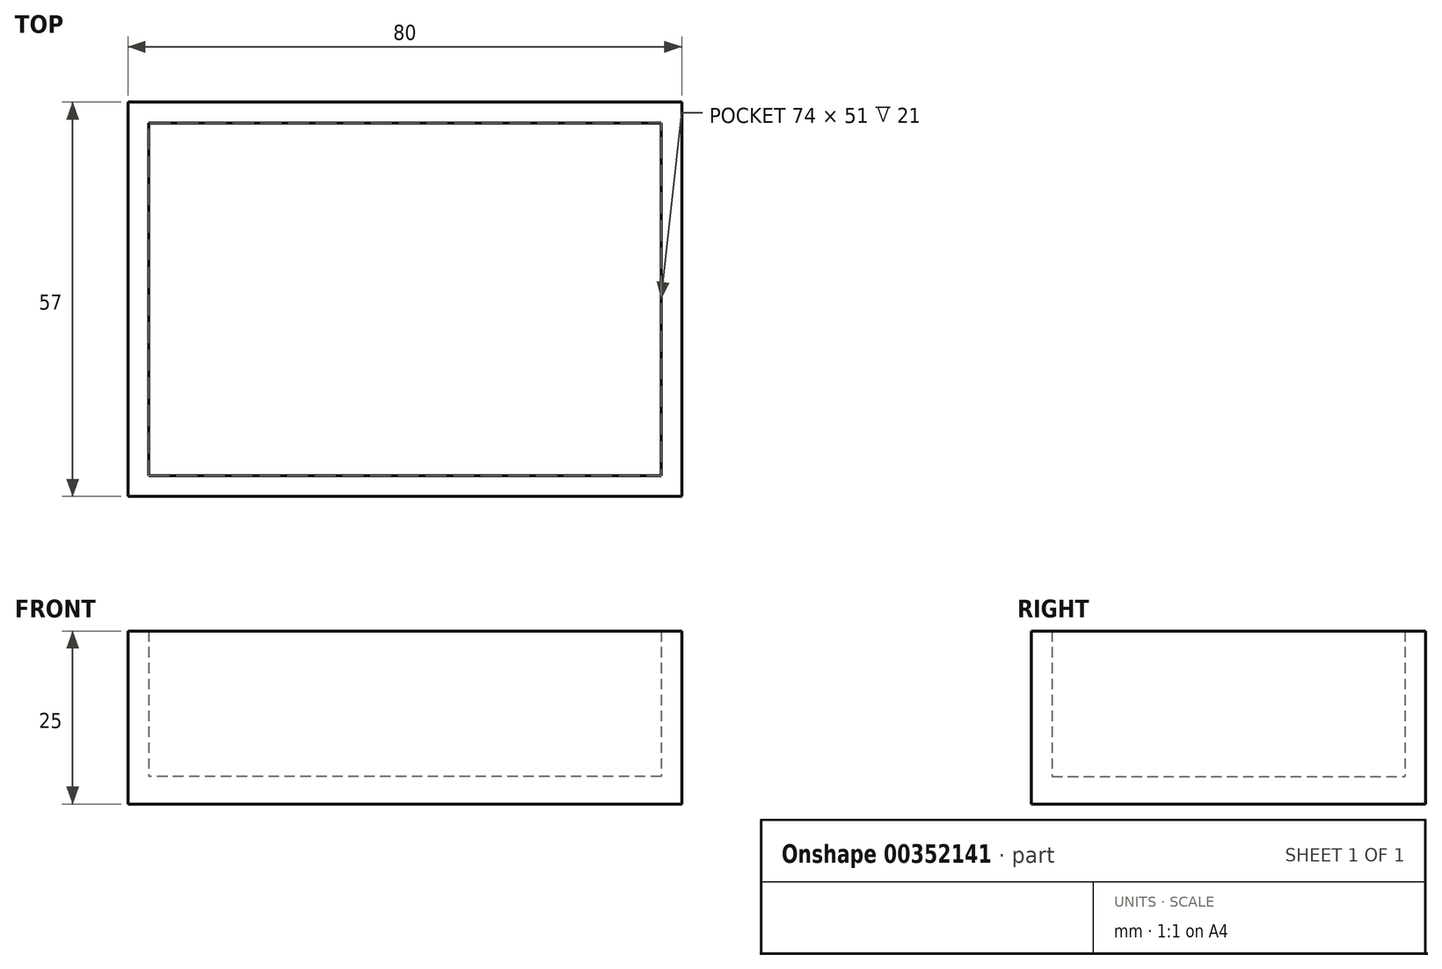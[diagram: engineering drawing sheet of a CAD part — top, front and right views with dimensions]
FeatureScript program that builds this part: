
annotation { "Feature Type Name" : "Feature", "Feature Type Description" : "" }
export const myFeature = defineFeature(function(context is Context, id is Id, definition is map)
    precondition{}
    {
        {
            var Q0;
            Q0=qCreatedBy(makeId("Top.planeOp"),FACE);
            var sketch = newSketch(context, id + "F0", { "sketchPlane" : qUnion([Q0])});
            skLineSegment(sketch, "E0.bottom", {"start": v(0, 0) * mm, "end": v(-80, 0) * mm});
            skLineSegment(sketch, "E0.left", {"start": v(0, 0) * mm, "end": v(0, 57) * mm});
            skPoint(sketch, "E1", {"position": v(-40, 28.5) * mm});
            skLineSegment(sketch, "E2.bottom", {"start": v(-77, 54) * mm, "end": v(-3, 54) * mm});
            skLineSegment(sketch, "E2.top", {"start": v(-77, 3) * mm, "end": v(-3, 3) * mm});
            skLineSegment(sketch, "E2.left", {"start": v(-77, 54) * mm, "end": v(-77, 3) * mm});
            skLineSegment(sketch, "E2.right", {"start": v(-3, 54) * mm, "end": v(-3, 3) * mm});
            skLineSegment(sketch, "E3.top", {"start": v(-80, 0) * mm, "end": v(0, 0) * mm});
            skLineSegment(sketch, "E3.right", {"start": v(0, 57) * mm, "end": v(0, 0) * mm});
            skPoint(sketch, "E4", {"position": v(0, 0) * mm});
            skLineSegment(sketch, "E5.top", {"start": v(-80, 57) * mm, "end": v(0, 57) * mm});
            skLineSegment(sketch, "E5.left", {"start": v(-80, 0) * mm, "end": v(-80, 57) * mm});
            skSolve(sketch);
        }
        {
            var Q0;
            Q0=makeQuery(id+"F0.imprint","IMPRINT",FACE,{"disambiguationData":[TD([[makeQuery(id+"F0.imprint","IMPRINT",EDGE,{"derivedFrom":sQuery(id+"F0.wireOp",EDGE,"E2.bottom")}),1.0]])]});
            var Q1;
            Q1=makeQuery(id+"F0.imprint","IMPRINT",FACE,{"disambiguationData":[TD([[makeQuery(id+"F0.imprint","IMPRINT",EDGE,{"derivedFrom":sQuery(id+"F0.wireOp",EDGE,"E2.bottom")}),-1.0]])]});
            extrude(context, id + "F1", {"entities" : qUnion([Q0, Q1]), "depth" : 4 * mm});
        }
        {
            var Q0;
            Q0=makeQuery(id+"F0.imprint","IMPRINT",FACE,{"disambiguationData":[TD([[makeQuery(id+"F0.imprint","IMPRINT",EDGE,{"derivedFrom":sQuery(id+"F0.wireOp",EDGE,"E2.bottom")}),1.0]])]});
            extrude(context, id + "F2", {"entities" : qUnion([Q0]), "operationType" : NewBodyOperationType.ADD, "depth" : 25 * mm});
        }
    });
